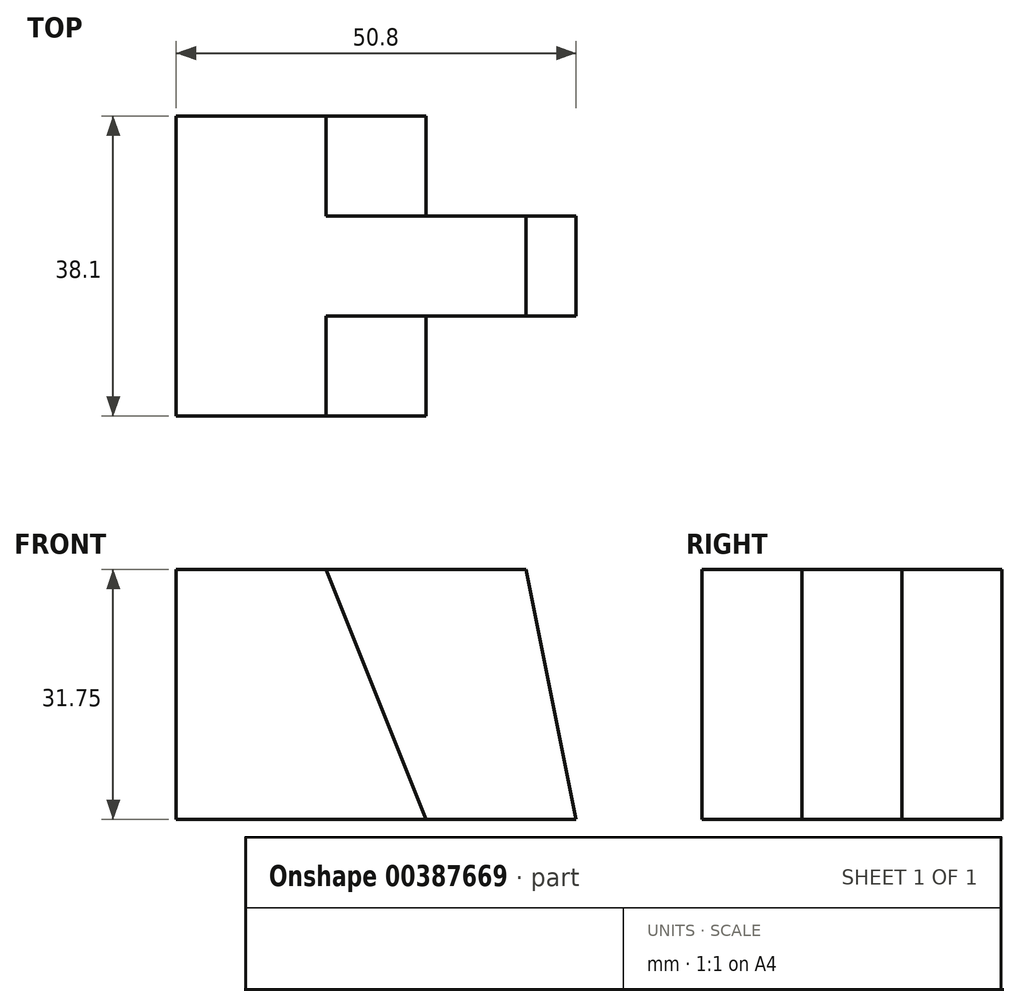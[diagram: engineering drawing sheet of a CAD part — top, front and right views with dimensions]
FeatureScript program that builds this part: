
annotation { "Feature Type Name" : "Feature", "Feature Type Description" : "" }
export const myFeature = defineFeature(function(context is Context, id is Id, definition is map)
    precondition{}
    {
        {
            var Q0;
            Q0=qCreatedBy(makeId("Top.planeOp"),FACE);
            var sketch = newSketch(context, id + "F0", { "sketchPlane" : qUnion([Q0])});
            skLineSegment(sketch, "E0", {"start": v(0, 0) * mm, "end": v(0, 38.1) * mm});
            skLineSegment(sketch, "E1", {"start": v(0, 38.1) * mm, "end": v(19.05, 38.1) * mm});
            skLineSegment(sketch, "E2", {"start": v(19.05, 38.1) * mm, "end": v(19.05, 25.4) * mm});
            skLineSegment(sketch, "E3", {"start": v(19.05, 25.4) * mm, "end": v(44.45, 25.4) * mm});
            skLineSegment(sketch, "E4", {"start": v(44.45, 25.4) * mm, "end": v(44.45, 12.7) * mm});
            skLineSegment(sketch, "E5", {"start": v(44.45, 12.7) * mm, "end": v(19.05, 12.7) * mm});
            skLineSegment(sketch, "E6", {"start": v(19.05, 12.7) * mm, "end": v(19.05, 0) * mm});
            skLineSegment(sketch, "E7", {"start": v(19.05, 0) * mm, "end": v(0, 0) * mm});
            skSolve(sketch);
        }
        {
            var Q0;
            Q0=makeQuery(id+"F0.imprint","IMPRINT",FACE,{"disambiguationData":[TD([[makeQuery(id+"F0.imprint","IMPRINT",EDGE,{"derivedFrom":sQuery(id+"F0.wireOp",EDGE,"E0")}),-1.0]])]});
            extrude(context, id + "F1", {"entities" : qUnion([Q0]), "depth" : 31.75 * mm});
        }
        {
            var Q0;
            Q0=makeQuery(id+"F1.opExtrude","SWEPT_FACE",FACE,{"disambiguationData":[OSD([sQuery(id+"F0.wireOp",EDGE,"E5")])]});
            var sketch = newSketch(context, id + "F2", { "sketchPlane" : qUnion([Q0])});
            skLineSegment(sketch, "E8", {"start": v(44.45, 31.75) * mm, "end": v(44.45, 0) * mm});
            skLineSegment(sketch, "E9", {"start": v(44.45, 0) * mm, "end": v(50.8, 0) * mm});
            skLineSegment(sketch, "E10", {"start": v(50.8, 0) * mm, "end": v(44.45, 31.75) * mm});
            skSolve(sketch);
        }
        {
            var Q0;
            Q0 = qSketchRegion(id + "F2", true);
            extrude(context, id + "F3", {"entities" : qUnion([Q0]), "operationType" : NewBodyOperationType.ADD, "oppositeDirection" : true, "depth" : 12.7 * mm});
        }
        {
            var Q0;
            Q0=makeQuery(id+"F1.opExtrude","SWEPT_FACE",FACE,{"disambiguationData":[OSD([sQuery(id+"F0.wireOp",EDGE,"E7")])]});
            var sketch = newSketch(context, id + "F4", { "sketchPlane" : qUnion([Q0])});
            skLineSegment(sketch, "E11", {"start": v(19.05, 31.75) * mm, "end": v(19.05, 0) * mm});
            skLineSegment(sketch, "E12", {"start": v(19.05, 0) * mm, "end": v(31.75, 0) * mm});
            skLineSegment(sketch, "E13", {"start": v(31.75, 0) * mm, "end": v(19.05, 31.75) * mm});
            skSolve(sketch);
        }
        {
            var Q0;
            Q0=makeQuery(id+"F4.imprint","IMPRINT",FACE,{"disambiguationData":[TD([[makeQuery(id+"F4.imprint","IMPRINT",EDGE,{"derivedFrom":sQuery(id+"F4.wireOp",EDGE,"E11")}),1.0]])]});
            extrude(context, id + "F5", {"entities" : qUnion([Q0]), "operationType" : NewBodyOperationType.ADD, "oppositeDirection" : true, "depth" : 38.1 * mm});
        }
    });
